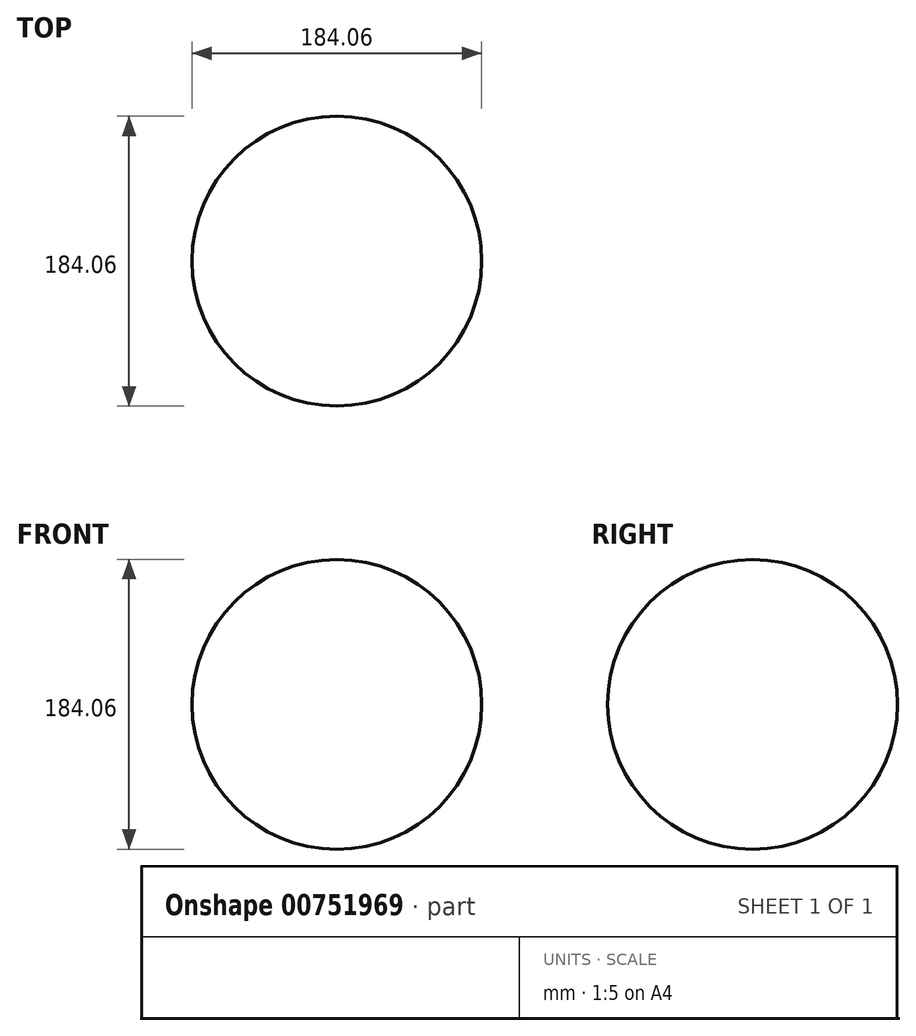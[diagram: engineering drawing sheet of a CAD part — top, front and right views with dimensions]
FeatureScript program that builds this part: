
annotation { "Feature Type Name" : "Feature", "Feature Type Description" : "" }
export const myFeature = defineFeature(function(context is Context, id is Id, definition is map)
    precondition{}
    {
        {
            var Q0;
            Q0=qCreatedBy(makeId("Front.planeOp"),FACE);
            var sketch = newSketch(context, id + "F0", { "sketchPlane" : qUnion([Q0])});
            skLineSegment(sketch, "E0", {"start": v(0, 85.26) * mm, "end": v(0, -98.8) * mm});
            skArc(sketch, "E1", {"start": v(0, -98.8) * mm, "mid": v(92.03, -6.77) * mm, "end": v(0, 85.26) * mm});
            skSolve(sketch);
        }
        {
            var Q0;
            Q0=makeQuery(id+"F0.imprint","IMPRINT",FACE,{"disambiguationData":[TD([[makeQuery(id+"F0.imprint","IMPRINT",EDGE,{"derivedFrom":sQuery(id+"F0.wireOp",EDGE,"E0")}),1.0]])]});
            var Q1;
            Q1=sQuery(id+"F0.wireOp",EDGE,"E0");
            revolve(context, id + "F1", {"surfaceOperationType" : NewSurfaceOperationType.NEW, "entities" : qUnion([Q0]), "axis" : qUnion([Q1]), "revolveType" : RevolveType.FULL});
        }
    });
